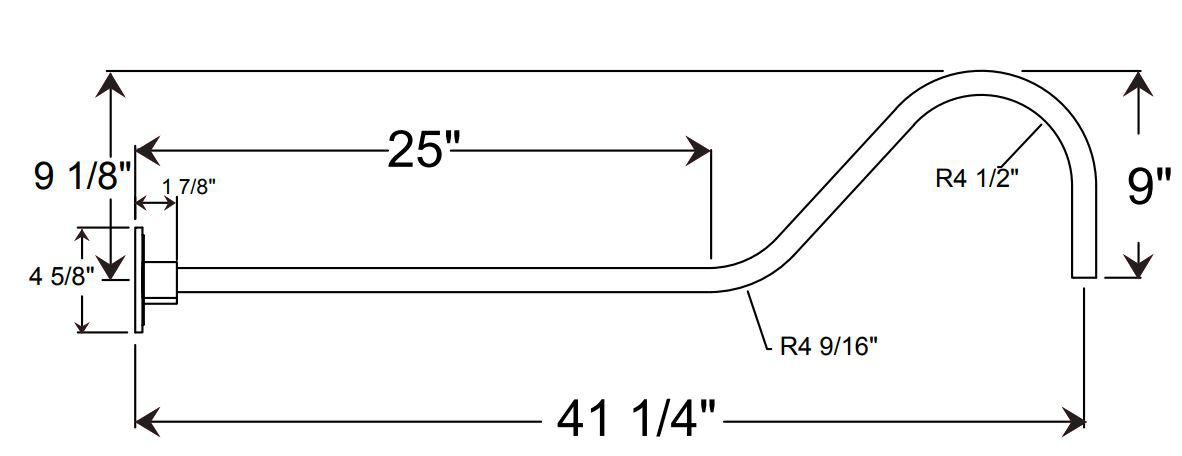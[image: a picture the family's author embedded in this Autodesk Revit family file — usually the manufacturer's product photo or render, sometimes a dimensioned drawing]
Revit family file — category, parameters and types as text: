
# Revit family: Magnolia(12,16,20,24) LED
name_source: partatom
category: Lighting Fixtures
units: mm (PartAtom-declared; Revit-internal decimal feet)

## family parameters
Always vertical = Yes
Cut with Voids When Loaded = No
Light Source = Yes
OmniClass Number = 23.80.70.00
OmniClass Title = Lighting
Part Type = Normal
Room Calculation Point = No
Round Connector Dimension = Use Diameter
Shared = No
Work Plane-Based = No

## types (4) — shared parameters
Body Colour = Spun aluminium
Body Material = body
CRI = >90
Color Filter = 16777215
Construction Material = Heavy Duty spun aluminum.
Default Elevation = 0' - 0"
Description = 120-277 Voltage
Dimming = 1%
Dimming Lamp Color Temperature Shift = <None>
Efficiency = 65-125 lumens per watt
Fixture Finish = Fixture Finish
INSIDE BODY = INSIDE BODY
Lamp = LED
Life = L70 50,000 hours
Load Classification = Lighting
Manufacturer = ANP Lighting
Power Factor = 1
Tilt Angle = 90.00°
URL = https://www.anplighting.com
Voltage = 277 V
Warranty = 5 year limited warranty

## per-type parameters (varying)
| type | Apparent Load | Fixture Diameter | Fixture Height | MDM12 | MDM16 | MDM20 | MDM24 | Photometric Web File | Wattage Comments | Weight |
| MDM12 | 10 VA | 1' - 0" | 1' - 0" | Yes | No | No | No | MDM12M010LD35K.IES | 10W | 5.5lbs |
| MDM16 | 16 VA | 1' - 4" | 1' - 4" | No | Yes | No | No | MDM16M016LD35K.IES | 16W | 6.0lbs |
| MDM20 | 16 VA | 1' - 8" | 1' - 8" | No | No | Yes | No | MDM20M016LD35K.IES | 16W | 6.5bs |
| MDM24 | 16 VA | 2' - 0" | 2' - 0" | No | No | No | Yes | MDM24M024LD35K.IES | 16W | 7.0bs |

note: column(s) folded — value = type name in every type: Model

## geometry (parser evidence)
native form markers: Sweep x22
no freeform markers — native parametric forms only
